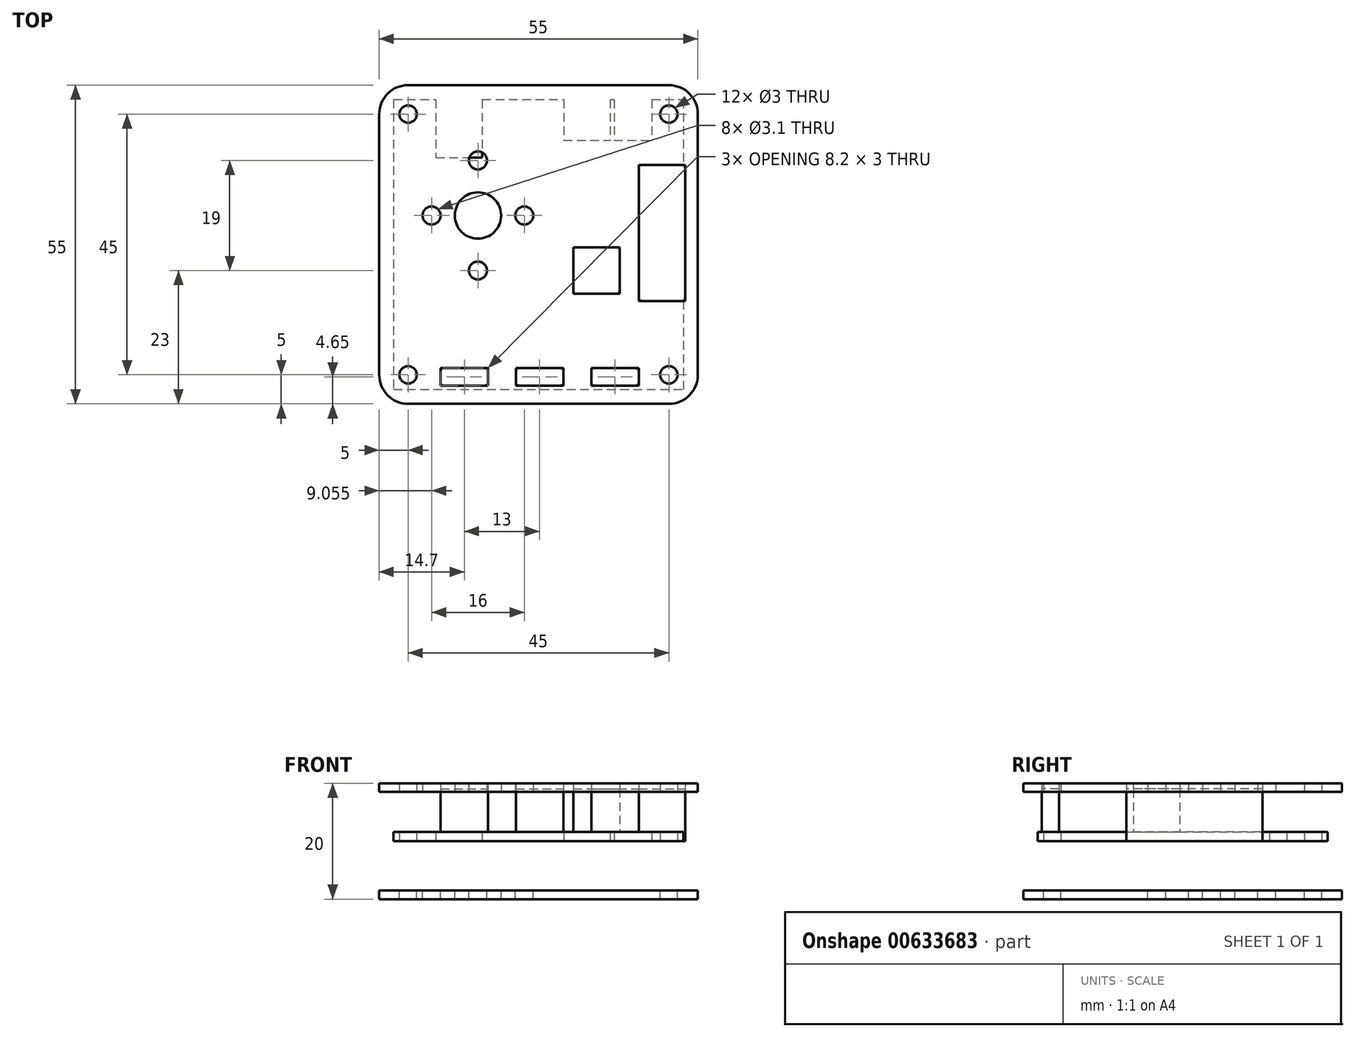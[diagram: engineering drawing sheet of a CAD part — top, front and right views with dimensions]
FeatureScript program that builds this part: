
annotation { "Feature Type Name" : "Feature", "Feature Type Description" : "" }
export const myFeature = defineFeature(function(context is Context, id is Id, definition is map)
    precondition{}
    {
        {
            var Q0;
            Q0=qCreatedBy(makeId("Top.planeOp"),FACE);
            var sketch = newSketch(context, id + "F0", { "sketchPlane" : qUnion([Q0])});
            skLineSegment(sketch, "E0.bottom", {"start": v(-25, 25) * mm, "end": v(25, 25) * mm});
            skLineSegment(sketch, "E0.top", {"start": v(-25, -25) * mm, "end": v(25, -25) * mm});
            skLineSegment(sketch, "E0.left", {"start": v(-25, 25) * mm, "end": v(-25, -25) * mm});
            skLineSegment(sketch, "E0.right", {"start": v(25, 25) * mm, "end": v(25, -25) * mm});
            skPoint(sketch, "E0.middle", {"position": v(0, 0) * mm});
            skCircle(sketch, "E1", {"center": v(-22.5, -22.5) * mm, "radius": 1.5 * mm});
            skCircle(sketch, "E2.0.1.0", {"center": v(-22.5, 22.5) * mm, "radius": 1.5 * mm});
            skCircle(sketch, "E2.1.0.0", {"center": v(22.5, -22.5) * mm, "radius": 1.5 * mm});
            skCircle(sketch, "E2.1.1.0", {"center": v(22.5, 22.5) * mm, "radius": 1.5 * mm});
            skLineSegment(sketch, "E2.direction1", {"start": v(-22.5, -22.5) * mm, "end": v(22.5, -22.5) * mm, "construction": true});
            skLineSegment(sketch, "E2.direction2", {"start": v(-22.5, -22.5) * mm, "end": v(-22.5, 22.5) * mm, "construction": true});
            skLineSegment(sketch, "E3.bottom", {"start": v(-17.7, 25) * mm, "end": v(-9.7, 25) * mm});
            skLineSegment(sketch, "E3.top", {"start": v(-17.7, 15) * mm, "end": v(-9.7, 15) * mm});
            skLineSegment(sketch, "E3.left", {"start": v(-17.7, 25) * mm, "end": v(-17.7, 15) * mm});
            skLineSegment(sketch, "E3.right", {"start": v(-9.7, 25) * mm, "end": v(-9.7, 15) * mm});
            skLineSegment(sketch, "E4.bottom", {"start": v(4.35, 25) * mm, "end": v(12.35, 25) * mm});
            skLineSegment(sketch, "E4.top", {"start": v(4.35, 18) * mm, "end": v(12.35, 18) * mm});
            skLineSegment(sketch, "E4.left", {"start": v(4.35, 25) * mm, "end": v(4.35, 18) * mm});
            skLineSegment(sketch, "E4.right", {"start": v(12.35, 25) * mm, "end": v(12.35, 18) * mm});
            skLineSegment(sketch, "E5.bottom", {"start": v(13.05, 25) * mm, "end": v(19.55, 25) * mm});
            skLineSegment(sketch, "E5.top", {"start": v(13.05, 18) * mm, "end": v(19.55, 18) * mm});
            skLineSegment(sketch, "E5.left", {"start": v(13.05, 25) * mm, "end": v(13.05, 18) * mm});
            skLineSegment(sketch, "E5.right", {"start": v(19.55, 25) * mm, "end": v(19.55, 18) * mm});
            skLineSegment(sketch, "E6.bottom", {"start": v(-16.9, -21.35) * mm, "end": v(-8.7, -21.35) * mm});
            skLineSegment(sketch, "E6.top", {"start": v(-16.9, -24.35) * mm, "end": v(-8.7, -24.35) * mm});
            skLineSegment(sketch, "E6.left", {"start": v(-16.9, -21.35) * mm, "end": v(-16.9, -24.35) * mm});
            skLineSegment(sketch, "E6.right", {"start": v(-8.7, -21.35) * mm, "end": v(-8.7, -24.35) * mm});
            skLineSegment(sketch, "E7.1.0.0", {"start": v(-3.9, -21.35) * mm, "end": v(-3.9, -24.35) * mm});
            skLineSegment(sketch, "E7.1.0.1", {"start": v(4.3, -21.35) * mm, "end": v(4.3, -24.35) * mm});
            skLineSegment(sketch, "E7.1.0.2", {"start": v(-3.9, -24.35) * mm, "end": v(4.3, -24.35) * mm});
            skLineSegment(sketch, "E7.1.0.3", {"start": v(-3.9, -21.35) * mm, "end": v(4.3, -21.35) * mm});
            skLineSegment(sketch, "E7.2.0.0", {"start": v(9.1, -21.35) * mm, "end": v(9.1, -24.35) * mm});
            skLineSegment(sketch, "E7.2.0.1", {"start": v(17.3, -21.35) * mm, "end": v(17.3, -24.35) * mm});
            skLineSegment(sketch, "E7.2.0.2", {"start": v(9.1, -24.35) * mm, "end": v(17.3, -24.35) * mm});
            skLineSegment(sketch, "E7.2.0.3", {"start": v(9.1, -21.35) * mm, "end": v(17.3, -21.35) * mm});
            skLineSegment(sketch, "E7.direction1", {"start": v(-16.9, -24.35) * mm, "end": v(-3.9, -24.35) * mm, "construction": true});
            skLineSegment(sketch, "E8.bottom", {"start": v(17.3, 13.75) * mm, "end": v(25.3, 13.75) * mm});
            skLineSegment(sketch, "E8.top", {"start": v(17.3, -9.75) * mm, "end": v(25.3, -9.75) * mm});
            skLineSegment(sketch, "E8.left", {"start": v(17.3, 13.75) * mm, "end": v(17.3, -9.75) * mm});
            skLineSegment(sketch, "E8.right", {"start": v(25.3, 13.75) * mm, "end": v(25.3, -9.75) * mm});
            skLineSegment(sketch, "E9.bottom", {"start": v(6, -0.5) * mm, "end": v(14, -0.5) * mm});
            skLineSegment(sketch, "E9.top", {"start": v(6, -8.5) * mm, "end": v(14, -8.5) * mm});
            skLineSegment(sketch, "E9.left", {"start": v(6, -0.5) * mm, "end": v(6, -8.5) * mm});
            skLineSegment(sketch, "E9.right", {"start": v(14, -0.5) * mm, "end": v(14, -8.5) * mm});
            skSolve(sketch);
        }
        {
            var Q0;
            {var subQ13=sQuery(id+"F0.wireOp",EDGE,"E0.top");Q0=makeQuery(id+"F0.imprint","IMPRINT",FACE,{"disambiguationData":[TD([[makeQuery(id+"F0.imprint","IMPRINT",EDGE,{"derivedFrom":subQ13}),1.0]])]});}
            var Q1;
            Q1=makeQuery(id+"F0.imprint","IMPRINT",FACE,{"disambiguationData":[TD([[makeQuery(id+"F0.imprint","IMPRINT",EDGE,{"derivedFrom":sQuery(id+"F0.wireOp",EDGE,"E3.bottom")}),-1.0]])]});
            var Q2;
            Q2=makeQuery(id+"F0.imprint","IMPRINT",FACE,{"disambiguationData":[TD([[makeQuery(id+"F0.imprint","IMPRINT",EDGE,{"derivedFrom":sQuery(id+"F0.wireOp",EDGE,"E4.bottom")}),-1.0]])]});
            var Q3;
            Q3=makeQuery(id+"F0.imprint","IMPRINT",FACE,{"disambiguationData":[TD([[makeQuery(id+"F0.imprint","IMPRINT",EDGE,{"derivedFrom":sQuery(id+"F0.wireOp",EDGE,"E5.bottom")}),-1.0]])]});
            var Q4;
            {var subQ5=sQuery(id+"F0.wireOp",EDGE,"E8.left");Q4=makeQuery(id+"F0.imprint","IMPRINT",FACE,{"disambiguationData":[TD([[makeQuery(id+"F0.imprint","IMPRINT",EDGE,{"derivedFrom":subQ5}),1.0]])]});}
            var Q5;
            Q5=makeQuery(id+"F0.imprint","IMPRINT",FACE,{"disambiguationData":[TD([[makeQuery(id+"F0.imprint","IMPRINT",EDGE,{"derivedFrom":sQuery(id+"F0.wireOp",EDGE,"E9.bottom")}),-1.0]])]});
            var Q6;
            Q6=makeQuery(id+"F0.imprint","IMPRINT",FACE,{"disambiguationData":[TD([[makeQuery(id+"F0.imprint","IMPRINT",EDGE,{"derivedFrom":sQuery(id+"F0.wireOp",EDGE,"E7.1.0.0")}),1.0]])]});
            var Q7;
            Q7=makeQuery(id+"F0.imprint","IMPRINT",FACE,{"disambiguationData":[TD([[makeQuery(id+"F0.imprint","IMPRINT",EDGE,{"derivedFrom":sQuery(id+"F0.wireOp",EDGE,"E6.bottom")}),-1.0]])]});
            var Q8;
            Q8=makeQuery(id+"F0.imprint","IMPRINT",FACE,{"disambiguationData":[TD([[makeQuery(id+"F0.imprint","IMPRINT",EDGE,{"derivedFrom":sQuery(id+"F0.wireOp",EDGE,"E7.2.0.0")}),1.0]])]});
            extrude(context, id + "F1", {"entities" : qUnion([Q0, Q1, Q2, Q3, Q4, Q5, Q6, Q7, Q8]), "depth" : 1.6 * mm, "offsetDistance" : 25 * mm});
        }
        {
            var Q0;
            {var subQ5=sQuery(id+"F0.wireOp",EDGE,"E8.left");Q0=makeQuery(id+"F0.imprint","IMPRINT",FACE,{"disambiguationData":[TD([[makeQuery(id+"F0.imprint","IMPRINT",EDGE,{"derivedFrom":subQ5}),1.0]])]});}
            var Q1;
            Q1=makeQuery(id+"F0.imprint","IMPRINT",FACE,{"disambiguationData":[TD([[makeQuery(id+"F0.imprint","IMPRINT",EDGE,{"derivedFrom":sQuery(id+"F0.wireOp",EDGE,"E9.bottom")}),-1.0]])]});
            var Q2;
            Q2=makeQuery(id+"F0.imprint","IMPRINT",FACE,{"disambiguationData":[TD([[makeQuery(id+"F0.imprint","IMPRINT",EDGE,{"derivedFrom":sQuery(id+"F0.wireOp",EDGE,"E7.2.0.0")}),1.0]])]});
            var Q3;
            Q3=makeQuery(id+"F0.imprint","IMPRINT",FACE,{"disambiguationData":[TD([[makeQuery(id+"F0.imprint","IMPRINT",EDGE,{"derivedFrom":sQuery(id+"F0.wireOp",EDGE,"E7.1.0.0")}),1.0]])]});
            var Q4;
            Q4=makeQuery(id+"F0.imprint","IMPRINT",FACE,{"disambiguationData":[TD([[makeQuery(id+"F0.imprint","IMPRINT",EDGE,{"derivedFrom":sQuery(id+"F0.wireOp",EDGE,"E6.bottom")}),-1.0]])]});
            var Q5;
            {var subQ5=sQuery(id+"F0.wireOp",EDGE,"E8.right");Q5=makeQuery(id+"F0.imprint","IMPRINT",FACE,{"disambiguationData":[TD([[makeQuery(id+"F0.imprint","IMPRINT",EDGE,{"derivedFrom":subQ5}),-1.0]])]});}
            extrude(context, id + "F2", {"entities" : qUnion([Q0, Q1, Q2, Q3, Q4, Q5]), "operationType" : NewBodyOperationType.ADD, "depth" : 9 * mm, "offsetDistance" : 25 * mm});
        }
        {
            var Q0;
            Q0=qCreatedBy(makeId("Top.planeOp"),FACE);
            var sketch = newSketch(context, id + "F3", { "sketchPlane" : qUnion([Q0])});
            skCircle(sketch, "E10.0", {"center": v(-22.5, 22.5) * mm, "radius": 1.5 * mm});
            skCircle(sketch, "E11.0", {"center": v(22.5, 22.5) * mm, "radius": 1.5 * mm});
            skCircle(sketch, "E12.0", {"center": v(-22.5, -22.5) * mm, "radius": 1.5 * mm});
            skCircle(sketch, "E13.0", {"center": v(22.5, -22.5) * mm, "radius": 1.5 * mm});
            skLineSegment(sketch, "E14.0.0", {"start": v(17.8, -9.75) * mm, "end": v(24.8, -9.75) * mm});
            skLineSegment(sketch, "E14.0.1", {"start": v(25.3, -9.25) * mm, "end": v(25.3, 13.25) * mm});
            skLineSegment(sketch, "E14.0.2", {"start": v(24.8, 13.75) * mm, "end": v(17.8, 13.75) * mm});
            skLineSegment(sketch, "E14.0.3", {"start": v(17.3, 13.25) * mm, "end": v(17.3, -9.25) * mm});
            skLineSegment(sketch, "E15.0.0", {"start": v(6, -1) * mm, "end": v(6, -8) * mm});
            skLineSegment(sketch, "E15.0.1", {"start": v(6.5, -8.5) * mm, "end": v(13.5, -8.5) * mm});
            skLineSegment(sketch, "E15.0.2", {"start": v(14, -8) * mm, "end": v(14, -1) * mm});
            skLineSegment(sketch, "E15.0.3", {"start": v(13.5, -0.5) * mm, "end": v(6.5, -0.5) * mm});
            skLineSegment(sketch, "E16.0.0", {"start": v(17.3, -23.85) * mm, "end": v(17.3, -21.85) * mm});
            skLineSegment(sketch, "E16.0.1", {"start": v(16.8, -21.35) * mm, "end": v(9.6, -21.35) * mm});
            skLineSegment(sketch, "E16.0.2", {"start": v(9.1, -21.85) * mm, "end": v(9.1, -23.85) * mm});
            skLineSegment(sketch, "E16.0.3", {"start": v(9.6, -24.35) * mm, "end": v(16.8, -24.35) * mm});
            skLineSegment(sketch, "E17.0.0", {"start": v(4.3, -23.85) * mm, "end": v(4.3, -21.85) * mm});
            skLineSegment(sketch, "E17.0.1", {"start": v(3.8, -21.35) * mm, "end": v(-3.4, -21.35) * mm});
            skLineSegment(sketch, "E17.0.2", {"start": v(-3.9, -21.85) * mm, "end": v(-3.9, -23.85) * mm});
            skLineSegment(sketch, "E17.0.3", {"start": v(-3.4, -24.35) * mm, "end": v(3.8, -24.35) * mm});
            skLineSegment(sketch, "E18.0.0", {"start": v(-16.9, -21.85) * mm, "end": v(-16.9, -23.85) * mm});
            skLineSegment(sketch, "E18.0.1", {"start": v(-16.4, -24.35) * mm, "end": v(-9.2, -24.35) * mm});
            skLineSegment(sketch, "E18.0.2", {"start": v(-8.7, -23.85) * mm, "end": v(-8.7, -21.85) * mm});
            skLineSegment(sketch, "E18.0.3", {"start": v(-9.2, -21.35) * mm, "end": v(-16.4, -21.35) * mm});
            skLineSegment(sketch, "E19.bottom", {"start": v(-22.5, 27.5) * mm, "end": v(22.5, 27.5) * mm});
            skLineSegment(sketch, "E19.top", {"start": v(-22.5, -27.5) * mm, "end": v(22.5, -27.5) * mm});
            skLineSegment(sketch, "E19.left", {"start": v(-27.5, 22.5) * mm, "end": v(-27.5, -22.5) * mm});
            skLineSegment(sketch, "E19.right", {"start": v(27.5, 22.5) * mm, "end": v(27.5, -22.5) * mm});
            skPoint(sketch, "E19.middle", {"position": v(0, 0) * mm});
            skPoint(sketch, "E20.visualSharp", {"position": v(-27.5, 27.5) * mm});
            skArc(sketch, "E20.filletArc", {"start": v(-22.5, 27.5) * mm, "mid": v(-26.04, 26.04) * mm, "end": v(-27.5, 22.5) * mm});
            skPoint(sketch, "E21.visualSharp", {"position": v(27.5, 27.5) * mm});
            skArc(sketch, "E21.filletArc", {"start": v(27.5, 22.5) * mm, "mid": v(26.04, 26.04) * mm, "end": v(22.5, 27.5) * mm});
            skPoint(sketch, "E22.visualSharp", {"position": v(-27.5, -27.5) * mm});
            skArc(sketch, "E22.filletArc", {"start": v(-27.5, -22.5) * mm, "mid": v(-26.04, -26.04) * mm, "end": v(-22.5, -27.5) * mm});
            skPoint(sketch, "E23.visualSharp", {"position": v(27.5, -27.5) * mm});
            skArc(sketch, "E23.filletArc", {"start": v(22.5, -27.5) * mm, "mid": v(26.04, -26.04) * mm, "end": v(27.5, -22.5) * mm});
            skPoint(sketch, "E24.visualSharp", {"position": v(6, -0.5) * mm});
            skArc(sketch, "E24.filletArc", {"start": v(6.5, -0.5) * mm, "mid": v(6.15, -0.65) * mm, "end": v(6, -1) * mm});
            skPoint(sketch, "E25.visualSharp", {"position": v(14, -0.5) * mm});
            skArc(sketch, "E25.filletArc", {"start": v(14, -1) * mm, "mid": v(13.85, -0.65) * mm, "end": v(13.5, -0.5) * mm});
            skPoint(sketch, "E26.visualSharp", {"position": v(6, -8.5) * mm});
            skArc(sketch, "E26.filletArc", {"start": v(6, -8) * mm, "mid": v(6.15, -8.35) * mm, "end": v(6.5, -8.5) * mm});
            skPoint(sketch, "E27.visualSharp", {"position": v(14, -8.5) * mm});
            skArc(sketch, "E27.filletArc", {"start": v(13.5, -8.5) * mm, "mid": v(13.85, -8.35) * mm, "end": v(14, -8) * mm});
            skPoint(sketch, "E28.visualSharp", {"position": v(17.3, 13.75) * mm});
            skArc(sketch, "E28.filletArc", {"start": v(17.8, 13.75) * mm, "mid": v(17.45, 13.6) * mm, "end": v(17.3, 13.25) * mm});
            skPoint(sketch, "E29.visualSharp", {"position": v(25.3, 13.75) * mm});
            skArc(sketch, "E29.filletArc", {"start": v(25.3, 13.25) * mm, "mid": v(25.15, 13.6) * mm, "end": v(24.8, 13.75) * mm});
            skPoint(sketch, "E30.visualSharp", {"position": v(17.3, -9.75) * mm});
            skArc(sketch, "E30.filletArc", {"start": v(17.3, -9.25) * mm, "mid": v(17.45, -9.6) * mm, "end": v(17.8, -9.75) * mm});
            skPoint(sketch, "E31.visualSharp", {"position": v(25.3, -9.75) * mm});
            skArc(sketch, "E31.filletArc", {"start": v(24.8, -9.75) * mm, "mid": v(25.15, -9.6) * mm, "end": v(25.3, -9.25) * mm});
            skPoint(sketch, "E32.visualSharp", {"position": v(-16.9, -21.35) * mm});
            skArc(sketch, "E32.filletArc", {"start": v(-16.4, -21.35) * mm, "mid": v(-16.75, -21.5) * mm, "end": v(-16.9, -21.85) * mm});
            skPoint(sketch, "E33.visualSharp", {"position": v(-8.7, -24.35) * mm});
            skArc(sketch, "E33.filletArc", {"start": v(-9.2, -24.35) * mm, "mid": v(-8.85, -24.2) * mm, "end": v(-8.7, -23.85) * mm});
            skPoint(sketch, "E34.visualSharp", {"position": v(-8.7, -21.35) * mm});
            skArc(sketch, "E34.filletArc", {"start": v(-8.7, -21.85) * mm, "mid": v(-8.85, -21.5) * mm, "end": v(-9.2, -21.35) * mm});
            skPoint(sketch, "E35.visualSharp", {"position": v(-16.9, -24.35) * mm});
            skArc(sketch, "E35.filletArc", {"start": v(-16.9, -23.85) * mm, "mid": v(-16.75, -24.2) * mm, "end": v(-16.4, -24.35) * mm});
            skPoint(sketch, "E36.visualSharp", {"position": v(-3.9, -24.35) * mm});
            skArc(sketch, "E36.filletArc", {"start": v(-3.9, -23.85) * mm, "mid": v(-3.75, -24.2) * mm, "end": v(-3.4, -24.35) * mm});
            skPoint(sketch, "E37.visualSharp", {"position": v(4.3, -21.35) * mm});
            skArc(sketch, "E37.filletArc", {"start": v(4.3, -21.85) * mm, "mid": v(4.15, -21.5) * mm, "end": v(3.8, -21.35) * mm});
            skPoint(sketch, "E38.visualSharp", {"position": v(9.1, -21.35) * mm});
            skArc(sketch, "E38.filletArc", {"start": v(9.6, -21.35) * mm, "mid": v(9.25, -21.5) * mm, "end": v(9.1, -21.85) * mm});
            skPoint(sketch, "E39.visualSharp", {"position": v(9.1, -24.35) * mm});
            skArc(sketch, "E39.filletArc", {"start": v(9.1, -23.85) * mm, "mid": v(9.25, -24.2) * mm, "end": v(9.6, -24.35) * mm});
            skPoint(sketch, "E40.visualSharp", {"position": v(17.3, -21.35) * mm});
            skArc(sketch, "E40.filletArc", {"start": v(17.3, -21.85) * mm, "mid": v(17.15, -21.5) * mm, "end": v(16.8, -21.35) * mm});
            skPoint(sketch, "E41.visualSharp", {"position": v(17.3, -24.35) * mm});
            skArc(sketch, "E41.filletArc", {"start": v(16.8, -24.35) * mm, "mid": v(17.15, -24.2) * mm, "end": v(17.3, -23.85) * mm});
            skPoint(sketch, "E42.visualSharp", {"position": v(-3.9, -21.35) * mm});
            skArc(sketch, "E42.filletArc", {"start": v(-3.4, -21.35) * mm, "mid": v(-3.75, -21.5) * mm, "end": v(-3.9, -21.85) * mm});
            skPoint(sketch, "E43.visualSharp", {"position": v(4.3, -24.35) * mm});
            skArc(sketch, "E43.filletArc", {"start": v(3.8, -24.35) * mm, "mid": v(4.15, -24.2) * mm, "end": v(4.3, -23.85) * mm});
            skCircle(sketch, "E44", {"center": v(-10.45, -4.5) * mm, "radius": 1.55 * mm});
            skCircle(sketch, "E45", {"center": v(-10.45, 14.5) * mm, "radius": 1.55 * mm});
            skCircle(sketch, "E46", {"center": v(-18.45, 5) * mm, "radius": 1.55 * mm});
            skCircle(sketch, "E47", {"center": v(-2.45, 5) * mm, "radius": 1.55 * mm});
            skCircle(sketch, "E48", {"center": v(-10.45, 5) * mm, "radius": 4 * mm});
            skLineSegment(sketch, "E49", {"start": v(-10.45, 14.5) * mm, "end": v(-10.45, -4.5) * mm, "construction": true});
            skLineSegment(sketch, "E50", {"start": v(-18.45, 5) * mm, "end": v(-2.45, 5) * mm, "construction": true});
            skCircle(sketch, "E51", {"center": v(-10.45, 5) * mm, "radius": 17.25 * mm, "construction": true});
            skCircle(sketch, "E52", {"center": v(-22.5, 22.5) * mm, "radius": 4 * mm, "construction": true});
            skSolve(sketch);
        }
        {
            var Q0;
            Q0=makeQuery(id+"F3.imprint","IMPRINT",FACE,{"disambiguationData":[TD([[makeQuery(id+"F3.imprint","IMPRINT",EDGE,{"derivedFrom":sQuery(id+"F3.wireOp",EDGE,"E10.0")}),-1.0]])]});
            extrude(context, id + "F4", {"entities" : qUnion([Q0]), "depth" : 10 * mm, "offsetDistance" : 25 * mm, "hasSecondDirection" : true, "secondDirectionOppositeDirection" : false, "secondDirectionDepth" : 8.5 * mm});
        }
        {
            var Q0;
            Q0=makeQuery(id+"F3.imprint","IMPRINT",FACE,{"disambiguationData":[TD([[makeQuery(id+"F3.imprint","IMPRINT",EDGE,{"derivedFrom":sQuery(id+"F3.wireOp",EDGE,"E10.0")}),-1.0]])]});
            var Q1;
            Q1=makeQuery(id+"F3.imprint","IMPRINT",FACE,{"disambiguationData":[TD([[makeQuery(id+"F3.imprint","IMPRINT",EDGE,{"derivedFrom":sQuery(id+"F3.wireOp",EDGE,"E14.0.0")}),1.0]])]});
            var Q2;
            Q2=makeQuery(id+"F3.imprint","IMPRINT",FACE,{"disambiguationData":[TD([[makeQuery(id+"F3.imprint","IMPRINT",EDGE,{"derivedFrom":sQuery(id+"F3.wireOp",EDGE,"E15.0.0")}),1.0]])]});
            var Q3;
            Q3=makeQuery(id+"F3.imprint","IMPRINT",FACE,{"disambiguationData":[TD([[makeQuery(id+"F3.imprint","IMPRINT",EDGE,{"derivedFrom":sQuery(id+"F3.wireOp",EDGE,"E16.0.0")}),1.0]])]});
            var Q4;
            Q4=makeQuery(id+"F3.imprint","IMPRINT",FACE,{"disambiguationData":[TD([[makeQuery(id+"F3.imprint","IMPRINT",EDGE,{"derivedFrom":sQuery(id+"F3.wireOp",EDGE,"E17.0.0")}),1.0]])]});
            var Q5;
            Q5=makeQuery(id+"F3.imprint","IMPRINT",FACE,{"disambiguationData":[TD([[makeQuery(id+"F3.imprint","IMPRINT",EDGE,{"derivedFrom":sQuery(id+"F3.wireOp",EDGE,"E18.0.0")}),1.0]])]});
            extrude(context, id + "F5", {"entities" : qUnion([Q0, Q1, Q2, Q3, Q4, Q5]), "oppositeDirection" : true, "depth" : 10 * mm, "offsetDistance" : 25 * mm, "hasSecondDirection" : true, "secondDirectionOppositeDirection" : true, "secondDirectionDepth" : 8.5 * mm});
        }
    });
